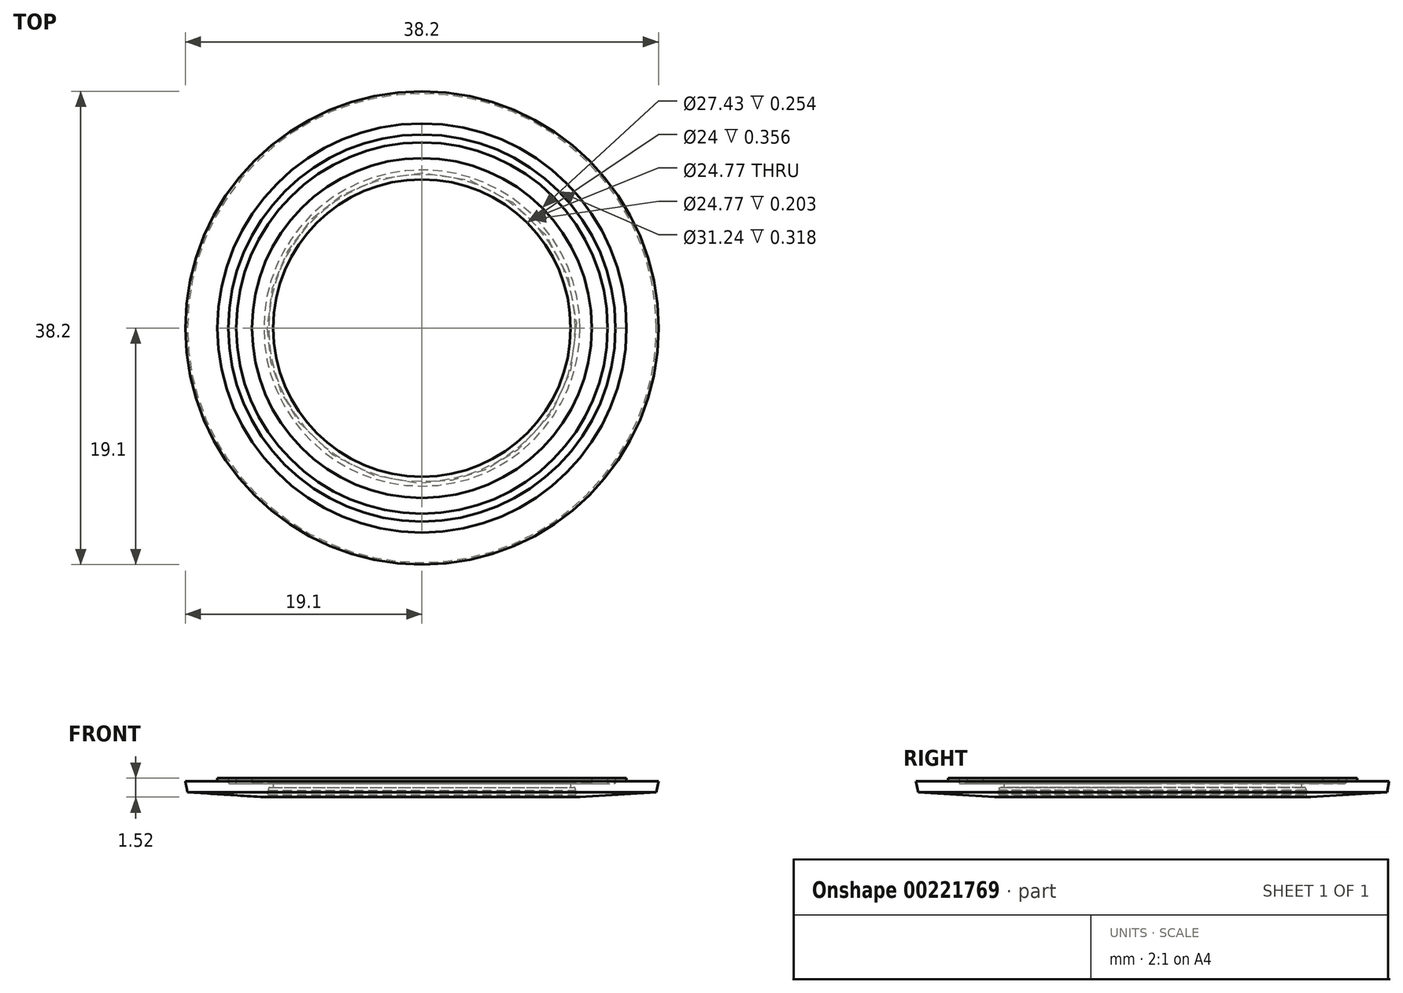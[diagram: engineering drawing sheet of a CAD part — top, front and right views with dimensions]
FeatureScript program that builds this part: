
annotation { "Feature Type Name" : "Feature", "Feature Type Description" : "" }
export const myFeature = defineFeature(function(context is Context, id is Id, definition is map)
    precondition{}
    {
        {
            var Q0;
            Q0=qCreatedBy(makeId("Front.planeOp"),FACE);
            var sketch = newSketch(context, id + "F0", { "sketchPlane" : qUnion([Q0])});
            skLineSegment(sketch, "E0", {"start": v(12, 0) * mm, "end": v(12, -0.36) * mm});
            skLineSegment(sketch, "E1", {"start": v(12, -0.36) * mm, "end": v(12.26, -0.36) * mm});
            skLineSegment(sketch, "E2", {"start": v(13.59, 0) * mm, "end": v(12, 0) * mm});
            skLineSegment(sketch, "E3", {"start": v(13.72, 0.13) * mm, "end": v(13.72, 0.38) * mm});
            skLineSegment(sketch, "E4", {"start": v(13.72, 0.38) * mm, "end": v(14.99, 0.38) * mm});
            skLineSegment(sketch, "E5", {"start": v(16.51, 0.38) * mm, "end": v(16.51, 0.25) * mm});
            skLineSegment(sketch, "E6", {"start": v(19.1, 0.13) * mm, "end": v(18.92, -0.74) * mm});
            skLineSegment(sketch, "E7", {"start": v(0, 0) * mm, "end": v(0, 2.46) * mm, "construction": true});
            skLineSegment(sketch, "E8", {"start": v(12.38, -0.58) * mm, "end": v(12.47, -0.67) * mm});
            skLineSegment(sketch, "E9", {"start": v(12.47, -0.85) * mm, "end": v(12.38, -0.94) * mm});
            skLineSegment(sketch, "E10", {"start": v(12.38, -1.14) * mm, "end": v(12.38, -0.94) * mm});
            skLineSegment(sketch, "E11.trimOffspring", {"start": v(12.38, -0.58) * mm, "end": v(12.38, -0.48) * mm});
            skPoint(sketch, "E12.visualSharp", {"position": v(12.56, -0.76) * mm});
            skArc(sketch, "E12.filletArc", {"start": v(12.47, -0.85) * mm, "mid": v(12.5, -0.76) * mm, "end": v(12.47, -0.67) * mm});
            skPoint(sketch, "E13.visualSharp", {"position": v(12.38, -0.36) * mm});
            skArc(sketch, "E13.filletArc", {"start": v(12.38, -0.48) * mm, "mid": v(12.35, -0.4) * mm, "end": v(12.26, -0.36) * mm});
            skPoint(sketch, "E14.visualSharp", {"position": v(13.72, 0) * mm});
            skArc(sketch, "E14.filletArc", {"start": v(13.59, 0) * mm, "mid": v(13.68, 0.04) * mm, "end": v(13.72, 0.13) * mm});
            skLineSegment(sketch, "E15", {"start": v(14.99, 0.38) * mm, "end": v(14.99, 0.06) * mm});
            skLineSegment(sketch, "E16", {"start": v(15.11, -0.06) * mm, "end": v(15.5, -0.06) * mm});
            skLineSegment(sketch, "E17", {"start": v(15.62, 0.06) * mm, "end": v(15.62, 0.38) * mm});
            skLineSegment(sketch, "E18.trimOffspring", {"start": v(15.62, 0.38) * mm, "end": v(16.51, 0.38) * mm});
            skPoint(sketch, "E19.visualSharp", {"position": v(14.99, -0.06) * mm});
            skArc(sketch, "E19.filletArc", {"start": v(14.99, 0.06) * mm, "mid": v(15.02, -0.03) * mm, "end": v(15.11, -0.06) * mm});
            skPoint(sketch, "E20.visualSharp", {"position": v(15.62, -0.06) * mm});
            skArc(sketch, "E20.filletArc", {"start": v(15.5, -0.06) * mm, "mid": v(15.58, -0.03) * mm, "end": v(15.62, 0.06) * mm});
            skLineSegment(sketch, "E21.0", {"start": v(16.64, 0.13) * mm, "end": v(19.1, 0.13) * mm});
            skPoint(sketch, "E22.visualSharp", {"position": v(16.51, 0.13) * mm});
            skArc(sketch, "E22.filletArc", {"start": v(16.51, 0.25) * mm, "mid": v(16.55, 0.16) * mm, "end": v(16.64, 0.13) * mm});
            skLineSegment(sketch, "E23", {"start": v(12.38, -1.14) * mm, "end": v(12.76, -1.14) * mm});
            skLineSegment(sketch, "E24", {"start": v(12.76, -1.14) * mm, "end": v(18.92, -0.74) * mm});
            skSolve(sketch);
        }
        {
            var Q0;
            Q0=makeQuery(id+"F0.imprint","IMPRINT",FACE,{"disambiguationData":[TD([[makeQuery(id+"F0.imprint","IMPRINT",EDGE,{"derivedFrom":sQuery(id+"F0.wireOp",EDGE,"E0")}),1.0]])]});
            var Q1;
            Q1=sQuery(id+"F0.wireOp",EDGE,"E7");
            revolve(context, id + "F1", {"entities" : qUnion([Q0]), "axis" : qUnion([Q1]), "revolveType" : RevolveType.FULL});
        }
    });
